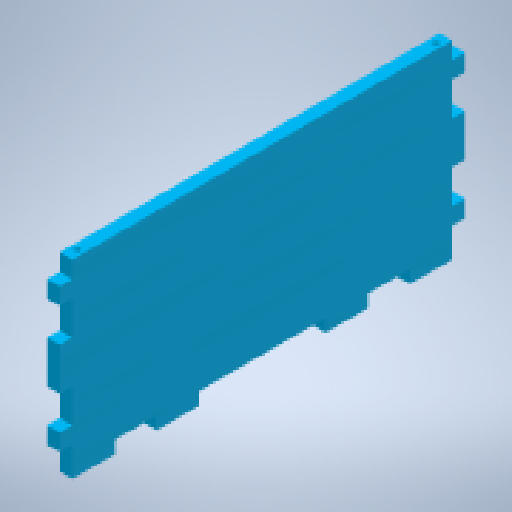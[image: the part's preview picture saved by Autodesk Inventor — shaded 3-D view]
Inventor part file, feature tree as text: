
AUTODESK INVENTOR PART (.ipt)
format: ipt  version: 2024.2 (Build 282272000, 272)  size: 306,176 bytes
history: native  units: mm
features: extrude x3, sketch x3, other x1
ambient origin geometry x8: Origin, YZ Plane, XZ Plane, XY Plane, X Axis, Y Axis, Z Axis, Center Point
bodies: Body1 (feature_tree)
feature tree (7):
  other  "Твердое тело1"
  extrude  "Выдавливание1"  Depth=180.0mm
  extrude  "Выдавливание4"  Depth=84.0mm
  extrude  "Выдавливание5"  Depth=90.0mm
  sketch  "Эскиз1"
  sketch  "Эскиз4"
  sketch  "Эскиз6"
